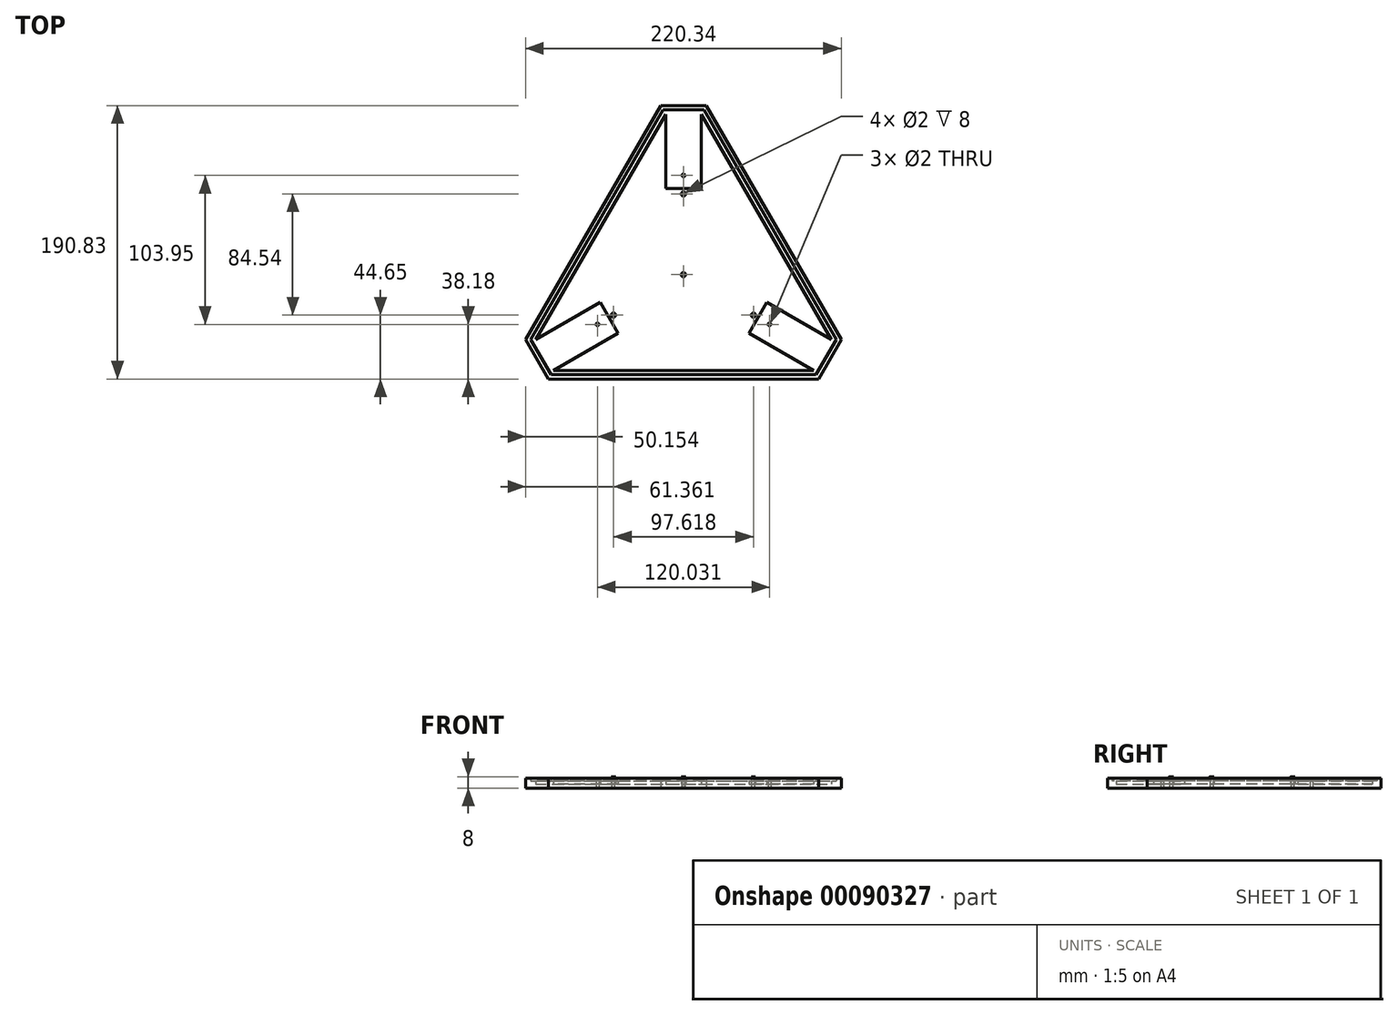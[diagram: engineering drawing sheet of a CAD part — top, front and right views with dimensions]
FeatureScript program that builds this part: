
annotation { "Feature Type Name" : "Feature", "Feature Type Description" : "" }
export const myFeature = defineFeature(function(context is Context, id is Id, definition is map)
    precondition{}
    {
        {
            var Q0;
            Q0=qCreatedBy(makeId("Top.planeOp"),FACE);
            var sketch = newSketch(context, id + "F0", { "sketchPlane" : qUnion([Q0])});
            skLineSegment(sketch, "E0.bottom", {"start": v(0, 0) * mm, "end": v(25, 0) * mm});
            skLineSegment(sketch, "E0.top", {"start": v(0, 52) * mm, "end": v(25, 52) * mm});
            skLineSegment(sketch, "E0.left", {"start": v(0, 0) * mm, "end": v(0, 52) * mm});
            skLineSegment(sketch, "E0.right", {"start": v(25, 0) * mm, "end": v(25, 52) * mm});
            skLineSegment(sketch, "E1", {"start": v(64.46, -90) * mm, "end": v(70.71, -79.17) * mm});
            skLineSegment(sketch, "E2", {"start": v(70.71, -79.17) * mm, "end": v(115.74, -105.17) * mm});
            skLineSegment(sketch, "E3", {"start": v(115.74, -105.17) * mm, "end": v(103.24, -126.83) * mm});
            skLineSegment(sketch, "E4", {"start": v(103.24, -126.83) * mm, "end": v(58.21, -100.83) * mm});
            skLineSegment(sketch, "E5", {"start": v(58.21, -100.83) * mm, "end": v(64.46, -90) * mm});
            skLineSegment(sketch, "E6", {"start": v(-39.46, -90) * mm, "end": v(-33.21, -100.83) * mm});
            skLineSegment(sketch, "E7", {"start": v(-33.21, -100.83) * mm, "end": v(-78.24, -126.83) * mm});
            skLineSegment(sketch, "E8", {"start": v(-78.24, -126.83) * mm, "end": v(-90.74, -105.17) * mm});
            skLineSegment(sketch, "E9", {"start": v(-90.74, -105.17) * mm, "end": v(-45.71, -79.17) * mm});
            skLineSegment(sketch, "E10", {"start": v(-45.71, -79.17) * mm, "end": v(-39.46, -90) * mm});
            skCircle(sketch, "E11", {"center": v(-36.3, -88.18) * mm, "radius": 1 * mm});
            skCircle(sketch, "E12", {"center": v(12.5, 9.3) * mm, "radius": 1 * mm});
            skCircle(sketch, "E13", {"center": v(72.52, -94.65) * mm, "radius": 1 * mm});
            skCircle(sketch, "E14", {"center": v(61.3, -88.18) * mm, "radius": 1 * mm});
            skCircle(sketch, "E15", {"center": v(12.5, -3.64) * mm, "radius": 1 * mm});
            skCircle(sketch, "E16", {"center": v(12.5, -60) * mm, "radius": 1 * mm});
            skCircle(sketch, "E17", {"center": v(-47.52, -94.65) * mm, "radius": 1 * mm});
            skLineSegment(sketch, "E18", {"start": v(-90.74, -105.17) * mm, "end": v(0, 52) * mm});
            skLineSegment(sketch, "E19", {"start": v(25, 52) * mm, "end": v(115.74, -105.17) * mm});
            skLineSegment(sketch, "E20", {"start": v(-78.24, -126.83) * mm, "end": v(103.24, -126.83) * mm});
            skLineSegment(sketch, "E21", {"start": v(-50.57, -23.59) * mm, "end": v(-97.67, -105.17) * mm});
            skLineSegment(sketch, "E22", {"start": v(-81.7, -132.83) * mm, "end": v(12.5, -132.83) * mm});
            skLineSegment(sketch, "E23", {"start": v(75.57, -23.59) * mm, "end": v(30.2, 55) * mm});
            skPoint(sketch, "E23.endSnap0", {"position": v(12.5, 52) * mm});
            skLineSegment(sketch, "E24", {"start": v(-5.2, 55) * mm, "end": v(-50.57, -23.59) * mm});
            skLineSegment(sketch, "E25", {"start": v(12.5, -132.83) * mm, "end": v(106.7, -132.83) * mm});
            skLineSegment(sketch, "E26", {"start": v(75.57, -23.59) * mm, "end": v(122.67, -105.17) * mm});
            skPoint(sketch, "E27.start.orphan", {"position": v(12.5, -126.83) * mm});
            skPoint(sketch, "E28.start.orphan", {"position": v(-45.37, -26.59) * mm});
            skPoint(sketch, "E29.start.orphan", {"position": v(70.37, -26.59) * mm});
            skLineSegment(sketch, "E30.trimOffspring", {"start": v(-35.44, -87.68) * mm, "end": v(-36.3, -88.18) * mm});
            skPoint(sketch, "E31.start.orphan", {"position": v(12.5, 0) * mm});
            skLineSegment(sketch, "E32", {"start": v(109.5, -116) * mm, "end": v(114.7, -119) * mm});
            skLineSegment(sketch, "E33", {"start": v(114.7, -119) * mm, "end": v(122.67, -105.17) * mm});
            skLineSegment(sketch, "E34", {"start": v(122.67, -105.17) * mm, "end": v(106.7, -132.83) * mm});
            skLineSegment(sketch, "E35", {"start": v(-84.5, -116) * mm, "end": v(-89.7, -119) * mm});
            skLineSegment(sketch, "E36", {"start": v(-89.7, -119) * mm, "end": v(-97.67, -105.17) * mm});
            skLineSegment(sketch, "E37", {"start": v(-97.67, -105.17) * mm, "end": v(-81.7, -132.83) * mm});
            skPoint(sketch, "E38.orphan", {"position": v(-113.64, -132.83) * mm});
            skLineSegment(sketch, "E39", {"start": v(12.5, 52) * mm, "end": v(12.5, 58) * mm});
            skPoint(sketch, "E40.orphan", {"position": v(12.5, 85.65) * mm});
            skLineSegment(sketch, "E41", {"start": v(-5.2, 55) * mm, "end": v(-3.46, 58) * mm});
            skLineSegment(sketch, "E42", {"start": v(30.2, 55) * mm, "end": v(28.46, 58) * mm});
            skLineSegment(sketch, "E43", {"start": v(12.5, 58) * mm, "end": v(28.46, 58) * mm});
            skLineSegment(sketch, "E44", {"start": v(28.46, 58) * mm, "end": v(-3.46, 58) * mm});
            skSolve(sketch);
        }
        {
            var Q0;
            Q0=makeQuery(id+"F0.imprint","IMPRINT",FACE,{"disambiguationData":[TD([[makeQuery(id+"F0.imprint","IMPRINT",EDGE,{"derivedFrom":sQuery(id+"F0.wireOp",EDGE,"E0.bottom")}),1.0]])]});
            var Q1;
            Q1=makeQuery(id+"F0.imprint","IMPRINT",FACE,{"disambiguationData":[TD([[makeQuery(id+"F0.imprint","IMPRINT",EDGE,{"derivedFrom":sQuery(id+"F0.wireOp",EDGE,"E1")}),-1.0]])]});
            var Q2;
            Q2=makeQuery(id+"F0.imprint","IMPRINT",FACE,{"disambiguationData":[TD([[makeQuery(id+"F0.imprint","IMPRINT",EDGE,{"derivedFrom":sQuery(id+"F0.wireOp",EDGE,"E0.top")}),1.0]])]});
            var Q3;
            Q3=makeQuery(id+"F0.imprint","IMPRINT",FACE,{"disambiguationData":[TD([[makeQuery(id+"F0.imprint","IMPRINT",EDGE,{"derivedFrom":sQuery(id+"F0.wireOp",EDGE,"E6")}),-1.0]])]});
            var Q4;
            {var subQ1=sQuery(id+"F0.wireOp",EDGE,"E20");Q4=makeQuery(id+"F0.imprint","IMPRINT",FACE,{"disambiguationData":[TD([[makeQuery(id+"F0.imprint","IMPRINT",EDGE,{"derivedFrom":subQ1}),-1.0]])]});}
            extrude(context, id + "F1", {"entities" : qUnion([Q0, Q1, Q2, Q3, Q4]), "depth" : 2 * mm});
        }
        {
            var Q0;
            Q0=makeQuery(id+"F1.opExtrude","CAP_FACE",FACE,{"disambiguationData":[OSD([sQuery(id+"F0.wireOp",EDGE,"E0.bottom"),sQuery(id+"F0.wireOp",EDGE,"E0.left"),sQuery(id+"F0.wireOp",EDGE,"E0.right"),sQuery(id+"F0.wireOp",EDGE,"E1"),sQuery(id+"F0.wireOp",EDGE,"E2"),sQuery(id+"F0.wireOp",EDGE,"E4"),sQuery(id+"F0.wireOp",EDGE,"E5"),sQuery(id+"F0.wireOp",EDGE,"E6"),sQuery(id+"F0.wireOp",EDGE,"E7"),sQuery(id+"F0.wireOp",EDGE,"E9"),sQuery(id+"F0.wireOp",EDGE,"E10"),sQuery(id+"F0.wireOp",EDGE,"E12"),sQuery(id+"F0.wireOp",EDGE,"E13"),sQuery(id+"F0.wireOp",EDGE,"E17"),sQuery(id+"F0.wireOp",EDGE,"E18"),sQuery(id+"F0.wireOp",EDGE,"E19"),sQuery(id+"F0.wireOp",EDGE,"E20"),sQuery(id+"F0.wireOp",EDGE,"E21"),sQuery(id+"F0.wireOp",EDGE,"E22"),sQuery(id+"F0.wireOp",EDGE,"E23"),sQuery(id+"F0.wireOp",EDGE,"E24"),sQuery(id+"F0.wireOp",EDGE,"E25"),sQuery(id+"F0.wireOp",EDGE,"E26")])],"isStart":true});
            var sketch = newSketch(context, id + "F2", { "sketchPlane" : qUnion([Q0])});
            skPoint(sketch, "E45.endSnap0", {"position": v(12.5, 0) * mm});
            skCircle(sketch, "E46", {"center": v(-36.3, 88.18) * mm, "radius": 1 * mm});
            skCircle(sketch, "E47", {"center": v(12.5, 60) * mm, "radius": 1 * mm});
            skCircle(sketch, "E48", {"center": v(61.3, 88.18) * mm, "radius": 1 * mm});
            skCircle(sketch, "E49", {"center": v(12.5, 3.64) * mm, "radius": 1 * mm});
            skPoint(sketch, "E50.orphan", {"position": v(-39.46, 90) * mm});
            skPoint(sketch, "E51.end.orphan", {"position": v(64.46, 90) * mm});
            skSolve(sketch);
        }
        {
            var Q0;
            Q0=makeQuery(id+"F2.imprint","IMPRINT",FACE,{"disambiguationData":[TD([[makeQuery(id+"F2.imprint","IMPRINT",EDGE,{"derivedFrom":sQuery(id+"F2.wireOp",EDGE,"E46")}),-1.0]])]});
            var Q1;
            Q1=makeQuery(id+"F2.imprint","IMPRINT",FACE,{"disambiguationData":[TD([[makeQuery(id+"F2.imprint","IMPRINT",EDGE,{"derivedFrom":makeQuery(id+"F1.opExtrude","CAP_EDGE",EDGE,{"disambiguationData":[OSD([sQuery(id+"F0.wireOp",EDGE,"E0.bottom")])],"isStart":true})}),-1.0]])]});
            extrude(context, id + "F3", {"entities" : qUnion([Q0, Q1]), "operationType" : NewBodyOperationType.ADD, "depth" : 3 * mm});
        }
        {
            var Q0;
            Q0=makeQuery(id+"F3.opExtrude","CAP_FACE",FACE,{"disambiguationData":[OSD([sQuery(id+"F0.wireOp",EDGE,"E12"),sQuery(id+"F0.wireOp",EDGE,"E13"),sQuery(id+"F0.wireOp",EDGE,"E17"),sQuery(id+"F0.wireOp",EDGE,"E21"),sQuery(id+"F0.wireOp",EDGE,"E22"),sQuery(id+"F0.wireOp",EDGE,"E23"),sQuery(id+"F0.wireOp",EDGE,"E24"),sQuery(id+"F0.wireOp",EDGE,"E25"),sQuery(id+"F0.wireOp",EDGE,"E26"),sQuery(id+"F2.wireOp",EDGE,"E46"),sQuery(id+"F2.wireOp",EDGE,"E47"),sQuery(id+"F2.wireOp",EDGE,"E48"),sQuery(id+"F2.wireOp",EDGE,"E49")])],"isStart":true});
            var sketch = newSketch(context, id + "F4", { "sketchPlane" : qUnion([Q0])});
            skCircle(sketch, "E52", {"center": v(12.5, -3.64) * mm, "radius": 1.5 * mm});
            skCircle(sketch, "E53", {"center": v(12.5, -60) * mm, "radius": 1.5 * mm});
            skCircle(sketch, "E54", {"center": v(-36.3, -88.18) * mm, "radius": 1.5 * mm});
            skCircle(sketch, "E55", {"center": v(61.3, -88.18) * mm, "radius": 1.5 * mm});
            skSolve(sketch);
        }
        {
            var Q0;
            Q0=makeQuery(id+"F4.imprint","IMPRINT",FACE,{"disambiguationData":[TD([[makeQuery(id+"F4.imprint","IMPRINT",EDGE,{"derivedFrom":sQuery(id+"F4.wireOp",EDGE,"E54")}),1.0]])]});
            var Q1;
            Q1=makeQuery(id+"F4.imprint","IMPRINT",FACE,{"disambiguationData":[TD([[makeQuery(id+"F4.imprint","IMPRINT",EDGE,{"derivedFrom":sQuery(id+"F4.wireOp",EDGE,"E55")}),1.0]])]});
            var Q2;
            Q2=makeQuery(id+"F4.imprint","IMPRINT",FACE,{"disambiguationData":[TD([[makeQuery(id+"F4.imprint","IMPRINT",EDGE,{"derivedFrom":sQuery(id+"F4.wireOp",EDGE,"E53")}),1.0]])]});
            var Q3;
            Q3=makeQuery(id+"F4.imprint","IMPRINT",FACE,{"disambiguationData":[TD([[makeQuery(id+"F4.imprint","IMPRINT",EDGE,{"derivedFrom":sQuery(id+"F4.wireOp",EDGE,"E52")}),1.0]])]});
            extrude(context, id + "F5", {"entities" : qUnion([Q0, Q1, Q2, Q3]), "operationType" : NewBodyOperationType.ADD, "depth" : 5 * mm});
        }
        {
            var Q0;
            Q0=makeQuery(id+"F1.opExtrude","CAP_FACE",FACE,{"disambiguationData":[OSD([sQuery(id+"F0.wireOp",EDGE,"E0.bottom"),sQuery(id+"F0.wireOp",EDGE,"E0.left"),sQuery(id+"F0.wireOp",EDGE,"E0.right"),sQuery(id+"F0.wireOp",EDGE,"E1"),sQuery(id+"F0.wireOp",EDGE,"E2"),sQuery(id+"F0.wireOp",EDGE,"E4"),sQuery(id+"F0.wireOp",EDGE,"E5"),sQuery(id+"F0.wireOp",EDGE,"E6"),sQuery(id+"F0.wireOp",EDGE,"E7"),sQuery(id+"F0.wireOp",EDGE,"E9"),sQuery(id+"F0.wireOp",EDGE,"E10"),sQuery(id+"F0.wireOp",EDGE,"E12"),sQuery(id+"F0.wireOp",EDGE,"E13"),sQuery(id+"F0.wireOp",EDGE,"E17"),sQuery(id+"F0.wireOp",EDGE,"E18"),sQuery(id+"F0.wireOp",EDGE,"E19"),sQuery(id+"F0.wireOp",EDGE,"E20"),sQuery(id+"F0.wireOp",EDGE,"E21"),sQuery(id+"F0.wireOp",EDGE,"E22"),sQuery(id+"F0.wireOp",EDGE,"E23"),sQuery(id+"F0.wireOp",EDGE,"E24"),sQuery(id+"F0.wireOp",EDGE,"E25"),sQuery(id+"F0.wireOp",EDGE,"E26"),sQuery(id+"F0.wireOp",EDGE,"E34"),sQuery(id+"F0.wireOp",EDGE,"E37"),sQuery(id+"F0.wireOp",EDGE,"E41"),sQuery(id+"F0.wireOp",EDGE,"E42"),sQuery(id+"F0.wireOp",EDGE,"E44")])],"isStart":false});
            var sketch = newSketch(context, id + "F6", { "sketchPlane" : qUnion([Q0])});
            skLineSegment(sketch, "E56", {"start": v(-45.37, -26.59) * mm, "end": v(-47.97, -25.09) * mm});
            skLineSegment(sketch, "E57", {"start": v(-47.97, -25.09) * mm, "end": v(-1.73, 55) * mm});
            skPoint(sketch, "E57.endSnap0", {"position": v(12.5, 58) * mm});
            skLineSegment(sketch, "E58", {"start": v(-47.97, -25.09) * mm, "end": v(-94.2, -105.17) * mm});
            skLineSegment(sketch, "E59", {"start": v(12.5, -126.83) * mm, "end": v(12.5, -129.83) * mm});
            skLineSegment(sketch, "E60", {"start": v(12.5, -129.83) * mm, "end": v(-79.98, -129.83) * mm});
            skLineSegment(sketch, "E61", {"start": v(-79.98, -129.83) * mm, "end": v(104.98, -129.83) * mm});
            skLineSegment(sketch, "E62", {"start": v(70.37, -26.59) * mm, "end": v(72.97, -25.09) * mm});
            skLineSegment(sketch, "E63", {"start": v(72.97, -25.09) * mm, "end": v(119.2, -105.17) * mm});
            skLineSegment(sketch, "E64", {"start": v(12.5, 55) * mm, "end": v(26.73, 55) * mm});
            skLineSegment(sketch, "E65", {"start": v(26.73, 55) * mm, "end": v(-1.73, 55) * mm});
            skLineSegment(sketch, "E66", {"start": v(-87.1, -117.5) * mm, "end": v(-94.2, -105.17) * mm});
            skLineSegment(sketch, "E67", {"start": v(-87.1, -117.5) * mm, "end": v(-79.98, -129.83) * mm});
            skLineSegment(sketch, "E68", {"start": v(112.1, -117.5) * mm, "end": v(104.98, -129.83) * mm});
            skLineSegment(sketch, "E69", {"start": v(112.1, -117.5) * mm, "end": v(119.2, -105.17) * mm});
            skPoint(sketch, "E70.start.orphan", {"position": v(-89.7, -119) * mm});
            skPoint(sketch, "E71.start.orphan", {"position": v(114.7, -119) * mm});
            skPoint(sketch, "E72.orphan", {"position": v(12.5, 79.65) * mm});
            skLineSegment(sketch, "E73", {"start": v(26.73, 55) * mm, "end": v(72.97, -25.09) * mm});
            skSolve(sketch);
        }
        {
            var Q0;
            {var subQ5=sQuery(id+"F6.wireOp",EDGE,"E57");Q0=makeQuery(id+"F6.imprint","IMPRINT",FACE,{"disambiguationData":[TD([[makeQuery(id+"F6.imprint","IMPRINT",EDGE,{"derivedFrom":subQ5}),1.0]])]});}
            extrude(context, id + "F7", {"entities" : qUnion([Q0]), "operationType" : NewBodyOperationType.ADD, "depth" : 2 * mm});
        }
    });
